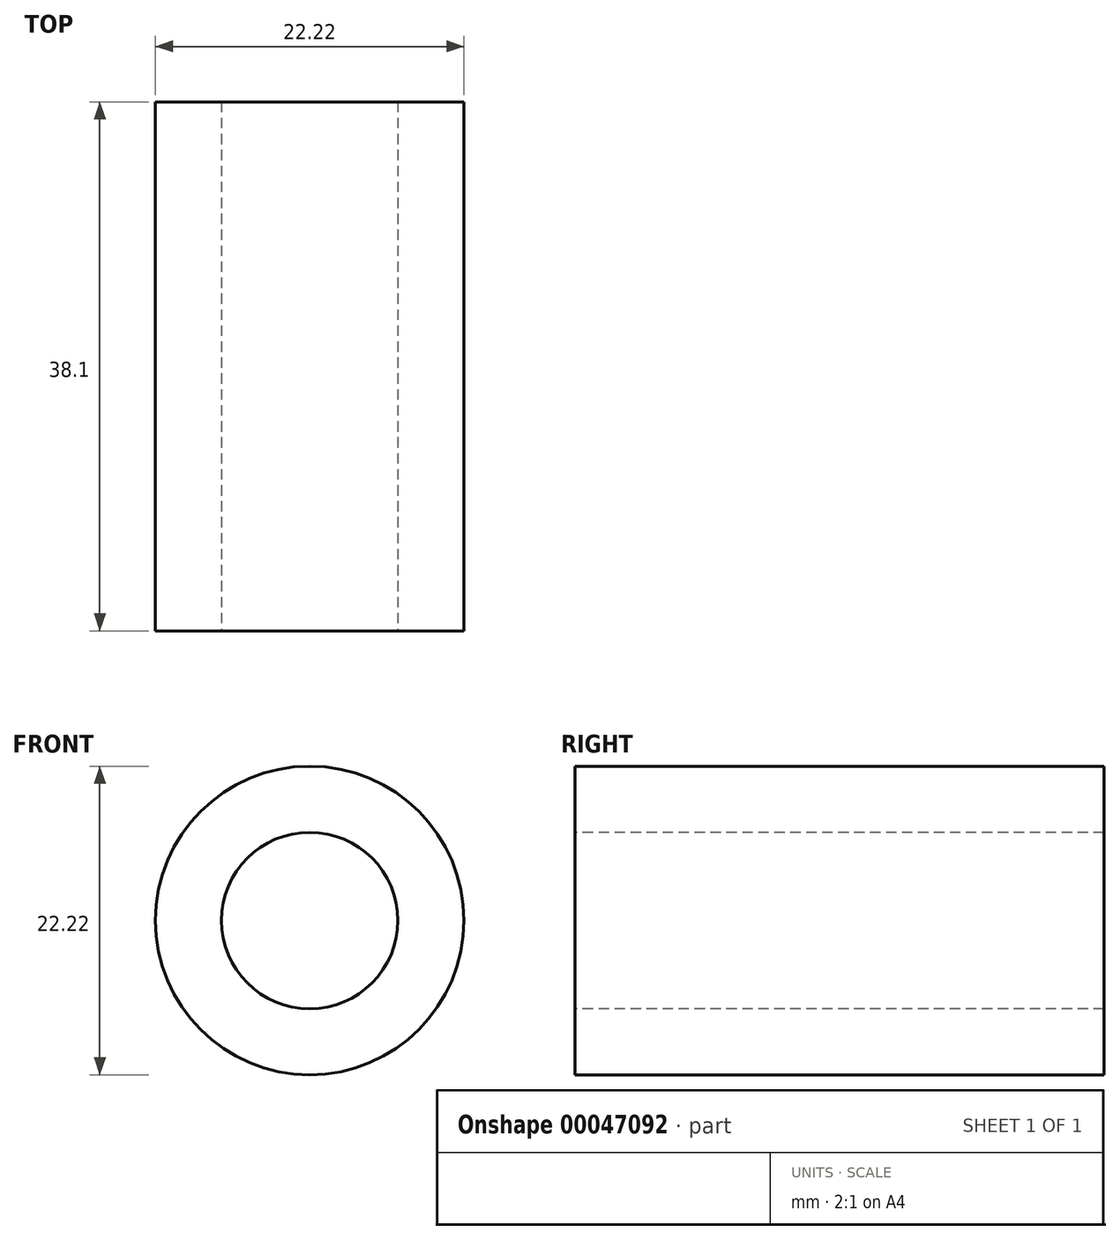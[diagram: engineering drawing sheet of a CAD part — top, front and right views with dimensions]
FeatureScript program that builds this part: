
annotation { "Feature Type Name" : "Feature", "Feature Type Description" : "" }
export const myFeature = defineFeature(function(context is Context, id is Id, definition is map)
    precondition{}
    {
        {
            var Q0;
            Q0=qCreatedBy(makeId("Front.planeOp"),FACE);
            var sketch = newSketch(context, id + "F0", { "sketchPlane" : qUnion([Q0])});
            skCircle(sketch, "E0", {"center": v(0, 0) * mm, "radius": 11.11 * mm});
            skSolve(sketch);
        }
        {
            var Q0;
            Q0 = qSketchRegion(id + "F0", true);
            extrude(context, id + "F1", {"entities" : qUnion([Q0]), "endBound" : BoundingType.SYMMETRIC, "depth" : 38.1 * mm});
        }
        {
            var Q0;
            Q0=makeQuery(id+"F1.opExtrude","CAP_FACE",FACE,{"disambiguationData":[OSD([sQuery(id+"F0.wireOp",EDGE,"E0")])],"isStart":false});
            var sketch = newSketch(context, id + "F2", { "sketchPlane" : qUnion([Q0])});
            skCircle(sketch, "E1", {"center": v(0, 0) * mm, "radius": 6.35 * mm});
            skSolve(sketch);
        }
        {
            var Q0;
            Q0 = qSketchRegion(id + "F2", true);
            extrude(context, id + "F3", {"entities" : qUnion([Q0]), "operationType" : NewBodyOperationType.REMOVE, "endBound" : BoundingType.THROUGH_ALL, "oppositeDirection" : true, "depth" : 25.4 * mm});
        }
    });
